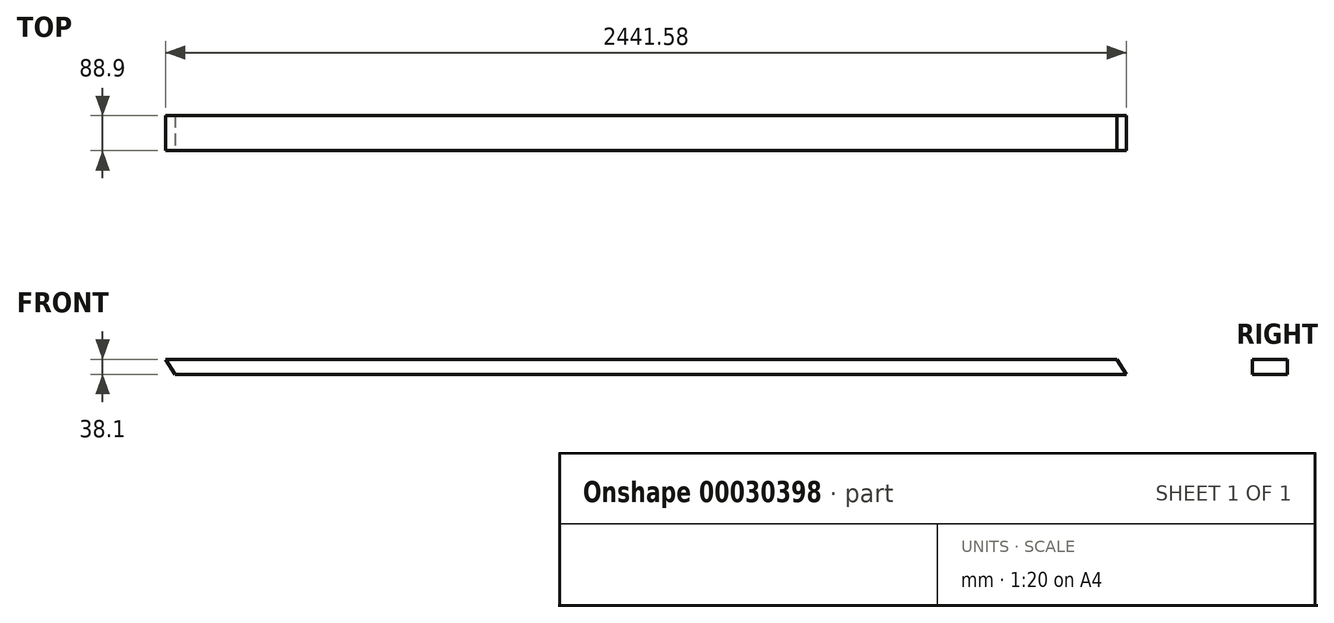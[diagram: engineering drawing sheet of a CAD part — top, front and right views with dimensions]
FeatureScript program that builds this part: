
annotation { "Feature Type Name" : "Feature", "Feature Type Description" : "" }
export const myFeature = defineFeature(function(context is Context, id is Id, definition is map)
    precondition{}
    {
        {
            var Q0;
            Q0=qCreatedBy(makeId("Top.planeOp"),FACE);
            var sketch = newSketch(context, id + "F0", { "sketchPlane" : qUnion([Q0])});
            skLineSegment(sketch, "E0.rect.left", {"start": v(1220.79, 44.45) * mm, "end": v(1220.79, -44.45) * mm});
            skLineSegment(sketch, "E0.rect.right", {"start": v(-1220.79, 44.45) * mm, "end": v(-1220.79, -44.45) * mm});
            skPoint(sketch, "E0.rect.middle", {"position": v(0, 0) * mm});
            skLineSegment(sketch, "E1", {"start": v(1220.79, 44.45) * mm, "end": v(69.34, 44.45) * mm});
            skLineSegment(sketch, "E2", {"start": v(-1220.79, 44.45) * mm, "end": v(69.34, 44.45) * mm});
            skLineSegment(sketch, "E3", {"start": v(-1220.79, -44.45) * mm, "end": v(-1164.72, -44.45) * mm});
            skLineSegment(sketch, "E4", {"start": v(1220.79, -44.45) * mm, "end": v(-1164.72, -44.45) * mm});
            skSolve(sketch);
        }
        {
            var Q0;
            Q0=qSketchRegion(id+"F0",true);
            extrude(context, id + "F1", {"entities" : qUnion([Q0]), "endBound" : BoundingType.SYMMETRIC, "depth" : 38.1 * mm});
        }
        {
            var Q0;
            Q0=qCreatedBy(makeId("Front.planeOp"),FACE);
            var sketch = newSketch(context, id + "F2", { "sketchPlane" : qUnion([Q0])});
            skLineSegment(sketch, "E5", {"start": v(1220.79, -19.05) * mm, "end": v(1196.76, 19.05) * mm});
            skLineSegment(sketch, "E6", {"start": v(-1196.76, -19.05) * mm, "end": v(-1220.79, 19.05) * mm});
            skLineSegment(sketch, "E7", {"start": v(-1220.79, 19.05) * mm, "end": v(-1220.79, -19.05) * mm});
            skLineSegment(sketch, "E8", {"start": v(-1220.79, -19.05) * mm, "end": v(-1196.76, -19.05) * mm});
            skLineSegment(sketch, "E9", {"start": v(1196.76, 19.05) * mm, "end": v(1220.79, 19.05) * mm});
            skLineSegment(sketch, "E10", {"start": v(1220.79, 19.05) * mm, "end": v(1220.79, -19.05) * mm});
            skSolve(sketch);
        }
        {
            var Q0;
            Q0=qSketchRegion(id+"F2",true);
            extrude(context, id + "F3", {"entities" : qUnion([Q0]), "operationType" : NewBodyOperationType.REMOVE, "endBound" : BoundingType.THROUGH_ALL, "oppositeDirection" : true, "depth" : 25.4 * mm, "hasSecondDirection" : true, "secondDirectionBound" : SecondDirectionBoundingType.THROUGH_ALL, "secondDirectionOppositeDirection" : false, "secondDirectionDepth" : 25.4 * mm});
        }
    });
